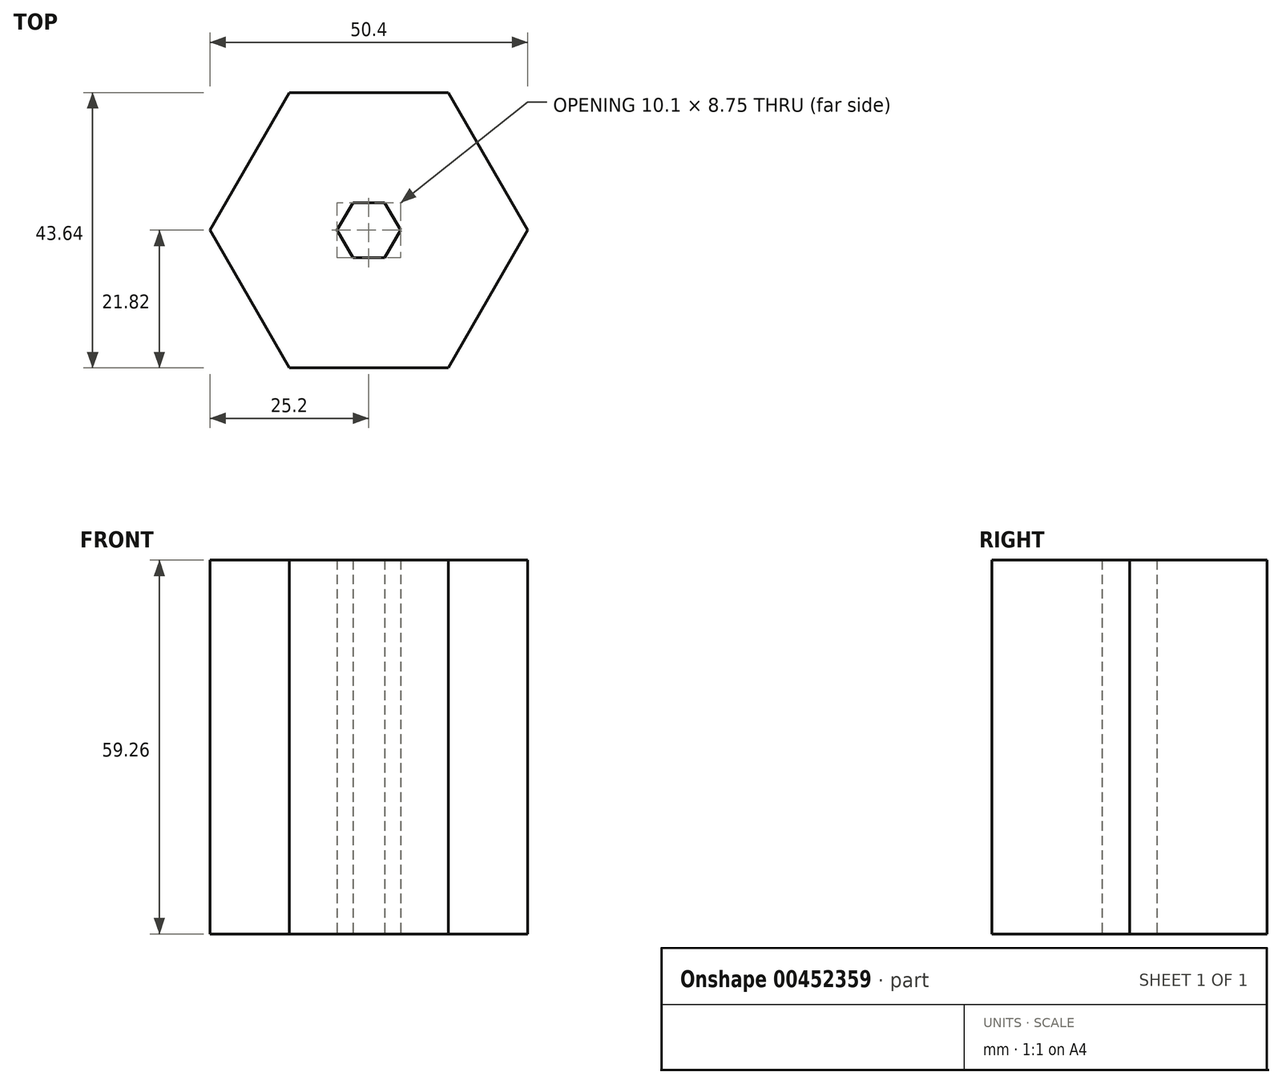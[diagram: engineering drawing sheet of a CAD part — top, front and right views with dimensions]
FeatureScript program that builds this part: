
annotation { "Feature Type Name" : "Feature", "Feature Type Description" : "" }
export const myFeature = defineFeature(function(context is Context, id is Id, definition is map)
    precondition{}
    {
        {
            var Q0;
            Q0=qCreatedBy(makeId("Top.planeOp"),FACE);
            var sketch = newSketch(context, id + "F0", { "sketchPlane" : qUnion([Q0])});
            skCircle(sketch, "E0.cCircle", {"center": v(0, 0) * mm, "radius": 21.82 * mm, "construction": true});
            skLineSegment(sketch, "E0.0", {"start": v(12.6, 21.82) * mm, "end": v(25.2, 0) * mm});
            skLineSegment(sketch, "E0.1", {"start": v(25.2, 0) * mm, "end": v(12.6, -21.82) * mm});
            skLineSegment(sketch, "E0.2", {"start": v(12.6, -21.82) * mm, "end": v(-12.6, -21.82) * mm});
            skLineSegment(sketch, "E0.3", {"start": v(-12.6, -21.82) * mm, "end": v(-25.2, 0) * mm});
            skLineSegment(sketch, "E0.4", {"start": v(-25.2, 0) * mm, "end": v(-12.6, 21.82) * mm});
            skLineSegment(sketch, "E0.5", {"start": v(-12.6, 21.82) * mm, "end": v(12.6, 21.82) * mm});
            skPoint(sketch, "E0.0.midPoint", {"position": v(18.9, 10.91) * mm});
            skCircle(sketch, "E1.cCircle", {"center": v(0, 0) * mm, "radius": 4.37 * mm, "construction": true});
            skLineSegment(sketch, "E1.0", {"start": v(2.53, 4.37) * mm, "end": v(5.05, 0) * mm});
            skLineSegment(sketch, "E1.1", {"start": v(5.05, 0) * mm, "end": v(2.53, -4.37) * mm});
            skLineSegment(sketch, "E1.2", {"start": v(2.53, -4.37) * mm, "end": v(-2.53, -4.37) * mm});
            skLineSegment(sketch, "E1.3", {"start": v(-2.53, -4.37) * mm, "end": v(-5.05, 0) * mm});
            skLineSegment(sketch, "E1.4", {"start": v(-5.05, 0) * mm, "end": v(-2.53, 4.37) * mm});
            skLineSegment(sketch, "E1.5", {"start": v(-2.52, 4.37) * mm, "end": v(2.53, 4.37) * mm});
            skPoint(sketch, "E1.0.midPoint", {"position": v(3.79, 2.19) * mm});
            skSolve(sketch);
        }
        {
            var Q0;
            Q0 = qSketchRegion(id + "F0", true);
            extrude(context, id + "F1", {"entities" : qUnion([Q0]), "depth" : 59.26 * mm});
        }
    });
